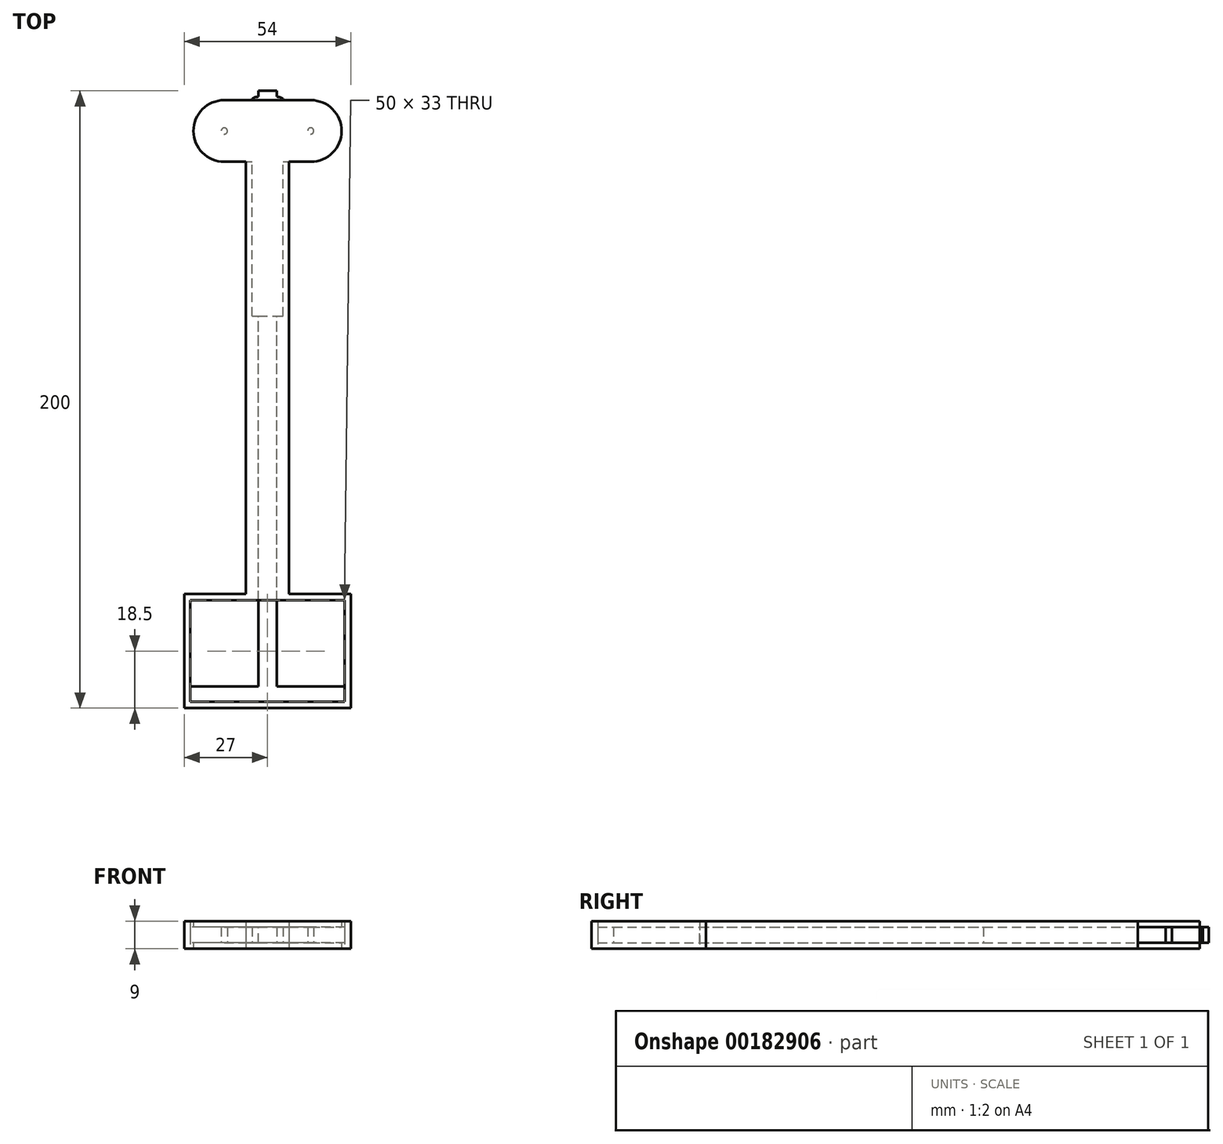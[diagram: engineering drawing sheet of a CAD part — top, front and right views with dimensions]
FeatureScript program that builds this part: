
annotation { "Feature Type Name" : "Feature", "Feature Type Description" : "" }
export const myFeature = defineFeature(function(context is Context, id is Id, definition is map)
    precondition{}
    {
        {
            var Q0;
            Q0=qCreatedBy(makeId("Top.planeOp"),FACE);
            var sketch = newSketch(context, id + "F0", { "sketchPlane" : qUnion([Q0])});
            skLineSegment(sketch, "E0.bottom", {"start": v(0, -180) * mm, "end": v(3, -180) * mm});
            skLineSegment(sketch, "E0.top", {"start": v(0, 13) * mm, "end": v(3, 13) * mm});
            skLineSegment(sketch, "E0.left", {"start": v(0, -180) * mm, "end": v(0, 13) * mm});
            skLineSegment(sketch, "E0.right", {"start": v(3, -180) * mm, "end": v(3, 13) * mm});
            skLineSegment(sketch, "E1", {"start": v(0, 10) * mm, "end": v(3, 10) * mm, "construction": true});
            skArc(sketch, "E2", {"start": v(3, 11.09) * mm, "mid": v(4.04, 10.94) * mm, "end": v(5, 10.5) * mm});
            skLineSegment(sketch, "E3", {"start": v(5, 10.5) * mm, "end": v(5, 10) * mm});
            skPoint(sketch, "E3.endSnap0", {"position": v(1.5, 10) * mm});
            skArc(sketch, "E4.MirrorCS", {"start": v(3, 8.91) * mm, "mid": v(4.04, 9.06) * mm, "end": v(5, 9.5) * mm});
            skLineSegment(sketch, "E5.MirrorCS", {"start": v(5, 9.5) * mm, "end": v(5, 10) * mm});
            skArc(sketch, "E6.1.0.0", {"start": v(3, 7.89) * mm, "mid": v(4.04, 7.74) * mm, "end": v(5, 7.3) * mm});
            skLineSegment(sketch, "E6.1.0.1", {"start": v(5, 7.3) * mm, "end": v(5, 6.8) * mm});
            skLineSegment(sketch, "E6.1.0.2", {"start": v(5, 6.3) * mm, "end": v(5, 6.8) * mm});
            skArc(sketch, "E6.1.0.3", {"start": v(3, 5.71) * mm, "mid": v(4.04, 5.86) * mm, "end": v(5, 6.3) * mm});
            skArc(sketch, "E6.2.0.0", {"start": v(3, 4.69) * mm, "mid": v(4.04, 4.54) * mm, "end": v(5, 4.1) * mm});
            skLineSegment(sketch, "E6.2.0.1", {"start": v(5, 4.1) * mm, "end": v(5, 3.6) * mm});
            skLineSegment(sketch, "E6.2.0.2", {"start": v(5, 3.1) * mm, "end": v(5, 3.6) * mm});
            skArc(sketch, "E6.2.0.3", {"start": v(3, 2.51) * mm, "mid": v(4.04, 2.66) * mm, "end": v(5, 3.1) * mm});
            skLineSegment(sketch, "E6.direction1", {"start": v(3, 7.39) * mm, "end": v(3, 4.19) * mm, "construction": true});
            skArc(sketch, "E7.0.3.0", {"start": v(3, 1.49) * mm, "mid": v(4.04, 1.34) * mm, "end": v(5, 0.9) * mm});
            skLineSegment(sketch, "E7.4.3.0", {"start": v(5, 0.9) * mm, "end": v(5, 0.4) * mm});
            skLineSegment(sketch, "E7.7.3.0", {"start": v(5, -0.1) * mm, "end": v(5, 0.4) * mm});
            skArc(sketch, "E7.10.3.0", {"start": v(3, -0.69) * mm, "mid": v(4.04, -0.54) * mm, "end": v(5, -0.1) * mm});
            skArc(sketch, "E7.0.4.0", {"start": v(3, -1.71) * mm, "mid": v(4.04, -1.86) * mm, "end": v(5, -2.3) * mm});
            skLineSegment(sketch, "E7.4.4.0", {"start": v(5, -2.3) * mm, "end": v(5, -2.8) * mm});
            skLineSegment(sketch, "E7.7.4.0", {"start": v(5, -3.3) * mm, "end": v(5, -2.8) * mm});
            skArc(sketch, "E7.10.4.0", {"start": v(3, -3.89) * mm, "mid": v(4.04, -3.74) * mm, "end": v(5, -3.3) * mm});
            skArc(sketch, "E7.0.5.0", {"start": v(3, -4.91) * mm, "mid": v(4.04, -5.06) * mm, "end": v(5, -5.5) * mm});
            skLineSegment(sketch, "E7.4.5.0", {"start": v(5, -5.5) * mm, "end": v(5, -6) * mm});
            skLineSegment(sketch, "E7.7.5.0", {"start": v(5, -6.5) * mm, "end": v(5, -6) * mm});
            skArc(sketch, "E7.10.5.0", {"start": v(3, -7.09) * mm, "mid": v(4.04, -6.94) * mm, "end": v(5, -6.5) * mm});
            skArc(sketch, "E7.0.6.0", {"start": v(3, -8.11) * mm, "mid": v(4.04, -8.26) * mm, "end": v(5, -8.7) * mm});
            skLineSegment(sketch, "E7.4.6.0", {"start": v(5, -8.7) * mm, "end": v(5, -9.2) * mm});
            skLineSegment(sketch, "E7.7.6.0", {"start": v(5, -9.7) * mm, "end": v(5, -9.2) * mm});
            skArc(sketch, "E7.10.6.0", {"start": v(3, -10.29) * mm, "mid": v(4.04, -10.14) * mm, "end": v(5, -9.7) * mm});
            skArc(sketch, "E7.0.7.0", {"start": v(3, -11.31) * mm, "mid": v(4.04, -11.46) * mm, "end": v(5, -11.9) * mm});
            skLineSegment(sketch, "E7.4.7.0", {"start": v(5, -11.9) * mm, "end": v(5, -12.4) * mm});
            skLineSegment(sketch, "E7.7.7.0", {"start": v(5, -12.9) * mm, "end": v(5, -12.4) * mm});
            skArc(sketch, "E7.10.7.0", {"start": v(3, -13.49) * mm, "mid": v(4.04, -13.34) * mm, "end": v(5, -12.9) * mm});
            skArc(sketch, "E7.0.8.0", {"start": v(3, -14.51) * mm, "mid": v(4.04, -14.66) * mm, "end": v(5, -15.1) * mm});
            skLineSegment(sketch, "E7.4.8.0", {"start": v(5, -15.1) * mm, "end": v(5, -15.6) * mm});
            skLineSegment(sketch, "E7.7.8.0", {"start": v(5, -16.1) * mm, "end": v(5, -15.6) * mm});
            skArc(sketch, "E7.10.8.0", {"start": v(3, -16.69) * mm, "mid": v(4.04, -16.54) * mm, "end": v(5, -16.1) * mm});
            skArc(sketch, "E7.0.9.0", {"start": v(3, -17.71) * mm, "mid": v(4.04, -17.86) * mm, "end": v(5, -18.3) * mm});
            skLineSegment(sketch, "E7.4.9.0", {"start": v(5, -18.3) * mm, "end": v(5, -18.8) * mm});
            skLineSegment(sketch, "E7.7.9.0", {"start": v(5, -19.3) * mm, "end": v(5, -18.8) * mm});
            skArc(sketch, "E7.10.9.0", {"start": v(3, -19.89) * mm, "mid": v(4.04, -19.74) * mm, "end": v(5, -19.3) * mm});
            skArc(sketch, "E7.0.10.0", {"start": v(3, -20.91) * mm, "mid": v(4.04, -21.06) * mm, "end": v(5, -21.5) * mm});
            skLineSegment(sketch, "E7.4.10.0", {"start": v(5, -21.5) * mm, "end": v(5, -22) * mm});
            skLineSegment(sketch, "E7.7.10.0", {"start": v(5, -22.5) * mm, "end": v(5, -22) * mm});
            skArc(sketch, "E7.10.10.0", {"start": v(3, -23.09) * mm, "mid": v(4.04, -22.94) * mm, "end": v(5, -22.5) * mm});
            skArc(sketch, "E7.0.11.0", {"start": v(3, -24.11) * mm, "mid": v(4.04, -24.26) * mm, "end": v(5, -24.7) * mm});
            skLineSegment(sketch, "E7.4.11.0", {"start": v(5, -24.7) * mm, "end": v(5, -25.2) * mm});
            skLineSegment(sketch, "E7.7.11.0", {"start": v(5, -25.7) * mm, "end": v(5, -25.2) * mm});
            skArc(sketch, "E7.10.11.0", {"start": v(3, -26.29) * mm, "mid": v(4.04, -26.14) * mm, "end": v(5, -25.7) * mm});
            skArc(sketch, "E7.0.12.0", {"start": v(3, -27.31) * mm, "mid": v(4.04, -27.46) * mm, "end": v(5, -27.9) * mm});
            skLineSegment(sketch, "E7.4.12.0", {"start": v(5, -27.9) * mm, "end": v(5, -28.4) * mm});
            skLineSegment(sketch, "E7.7.12.0", {"start": v(5, -28.9) * mm, "end": v(5, -28.4) * mm});
            skArc(sketch, "E7.10.12.0", {"start": v(3, -29.49) * mm, "mid": v(4.04, -29.34) * mm, "end": v(5, -28.9) * mm});
            skArc(sketch, "E7.0.13.0", {"start": v(3, -30.51) * mm, "mid": v(4.04, -30.66) * mm, "end": v(5, -31.1) * mm});
            skLineSegment(sketch, "E7.4.13.0", {"start": v(5, -31.1) * mm, "end": v(5, -31.6) * mm});
            skLineSegment(sketch, "E7.7.13.0", {"start": v(5, -32.1) * mm, "end": v(5, -31.6) * mm});
            skArc(sketch, "E7.10.13.0", {"start": v(3, -32.69) * mm, "mid": v(4.04, -32.54) * mm, "end": v(5, -32.1) * mm});
            skArc(sketch, "E7.0.14.0", {"start": v(3, -33.71) * mm, "mid": v(4.04, -33.86) * mm, "end": v(5, -34.3) * mm});
            skLineSegment(sketch, "E7.4.14.0", {"start": v(5, -34.3) * mm, "end": v(5, -34.8) * mm});
            skLineSegment(sketch, "E7.7.14.0", {"start": v(5, -35.3) * mm, "end": v(5, -34.8) * mm});
            skArc(sketch, "E7.10.14.0", {"start": v(3, -35.89) * mm, "mid": v(4.04, -35.74) * mm, "end": v(5, -35.3) * mm});
            skArc(sketch, "E7.0.15.0", {"start": v(3, -36.91) * mm, "mid": v(4.04, -37.06) * mm, "end": v(5, -37.5) * mm});
            skLineSegment(sketch, "E7.4.15.0", {"start": v(5, -37.5) * mm, "end": v(5, -38) * mm});
            skLineSegment(sketch, "E7.7.15.0", {"start": v(5, -38.5) * mm, "end": v(5, -38) * mm});
            skArc(sketch, "E7.10.15.0", {"start": v(3, -39.09) * mm, "mid": v(4.04, -38.94) * mm, "end": v(5, -38.5) * mm});
            skSolve(sketch);
        }
        {
            var Q0;
            Q0 = qSketchRegion(id + "F0", true);
            extrude(context, id + "F1", {"entities" : qUnion([Q0]), "depth" : 5 * mm});
        }
        {
            var Q0;
            Q0=makeQuery(id+"F1.opExtrude","SWEPT_BODY",BODY,{"disambiguationData":[OSD([sQuery(id+"F0.wireOp",EDGE,"E0.bottom"),sQuery(id+"F0.wireOp",EDGE,"E0.top"),sQuery(id+"F0.wireOp",EDGE,"E0.left"),sQuery(id+"F0.wireOp",EDGE,"E0.right"),sQuery(id+"F0.wireOp",EDGE,"E2"),sQuery(id+"F0.wireOp",EDGE,"E3"),sQuery(id+"F0.wireOp",EDGE,"E4.MirrorCS"),sQuery(id+"F0.wireOp",EDGE,"E5.MirrorCS"),sQuery(id+"F0.wireOp",EDGE,"E6.1.0.0"),sQuery(id+"F0.wireOp",EDGE,"E6.1.0.1"),sQuery(id+"F0.wireOp",EDGE,"E6.1.0.2"),sQuery(id+"F0.wireOp",EDGE,"E6.1.0.3"),sQuery(id+"F0.wireOp",EDGE,"E6.2.0.0"),sQuery(id+"F0.wireOp",EDGE,"E6.2.0.1"),sQuery(id+"F0.wireOp",EDGE,"E6.2.0.2"),sQuery(id+"F0.wireOp",EDGE,"E6.2.0.3"),sQuery(id+"F0.wireOp",EDGE,"E7.0.3.0"),sQuery(id+"F0.wireOp",EDGE,"E7.4.3.0"),sQuery(id+"F0.wireOp",EDGE,"E7.7.3.0"),sQuery(id+"F0.wireOp",EDGE,"E7.10.3.0"),sQuery(id+"F0.wireOp",EDGE,"E7.0.4.0"),sQuery(id+"F0.wireOp",EDGE,"E7.4.4.0"),sQuery(id+"F0.wireOp",EDGE,"E7.7.4.0"),sQuery(id+"F0.wireOp",EDGE,"E7.10.4.0"),sQuery(id+"F0.wireOp",EDGE,"E7.0.5.0"),sQuery(id+"F0.wireOp",EDGE,"E7.4.5.0"),sQuery(id+"F0.wireOp",EDGE,"E7.7.5.0"),sQuery(id+"F0.wireOp",EDGE,"E7.10.5.0"),sQuery(id+"F0.wireOp",EDGE,"E7.0.6.0"),sQuery(id+"F0.wireOp",EDGE,"E7.4.6.0"),sQuery(id+"F0.wireOp",EDGE,"E7.7.6.0"),sQuery(id+"F0.wireOp",EDGE,"E7.10.6.0"),sQuery(id+"F0.wireOp",EDGE,"E7.0.7.0"),sQuery(id+"F0.wireOp",EDGE,"E7.4.7.0"),sQuery(id+"F0.wireOp",EDGE,"E7.7.7.0"),sQuery(id+"F0.wireOp",EDGE,"E7.10.7.0"),sQuery(id+"F0.wireOp",EDGE,"E7.0.8.0"),sQuery(id+"F0.wireOp",EDGE,"E7.4.8.0"),sQuery(id+"F0.wireOp",EDGE,"E7.7.8.0"),sQuery(id+"F0.wireOp",EDGE,"E7.10.8.0"),sQuery(id+"F0.wireOp",EDGE,"E7.0.9.0"),sQuery(id+"F0.wireOp",EDGE,"E7.4.9.0"),sQuery(id+"F0.wireOp",EDGE,"E7.7.9.0"),sQuery(id+"F0.wireOp",EDGE,"E7.10.9.0"),sQuery(id+"F0.wireOp",EDGE,"E7.0.10.0"),sQuery(id+"F0.wireOp",EDGE,"E7.4.10.0"),sQuery(id+"F0.wireOp",EDGE,"E7.7.10.0"),sQuery(id+"F0.wireOp",EDGE,"E7.10.10.0"),sQuery(id+"F0.wireOp",EDGE,"E7.0.11.0"),sQuery(id+"F0.wireOp",EDGE,"E7.4.11.0"),sQuery(id+"F0.wireOp",EDGE,"E7.7.11.0"),sQuery(id+"F0.wireOp",EDGE,"E7.10.11.0"),sQuery(id+"F0.wireOp",EDGE,"E7.0.12.0"),sQuery(id+"F0.wireOp",EDGE,"E7.4.12.0"),sQuery(id+"F0.wireOp",EDGE,"E7.7.12.0"),sQuery(id+"F0.wireOp",EDGE,"E7.10.12.0"),sQuery(id+"F0.wireOp",EDGE,"E7.0.13.0"),sQuery(id+"F0.wireOp",EDGE,"E7.4.13.0"),sQuery(id+"F0.wireOp",EDGE,"E7.7.13.0"),sQuery(id+"F0.wireOp",EDGE,"E7.10.13.0"),sQuery(id+"F0.wireOp",EDGE,"E7.0.14.0"),sQuery(id+"F0.wireOp",EDGE,"E7.4.14.0"),sQuery(id+"F0.wireOp",EDGE,"E7.7.14.0"),sQuery(id+"F0.wireOp",EDGE,"E7.10.14.0"),sQuery(id+"F0.wireOp",EDGE,"E7.0.15.0"),sQuery(id+"F0.wireOp",EDGE,"E7.4.15.0"),sQuery(id+"F0.wireOp",EDGE,"E7.7.15.0"),sQuery(id+"F0.wireOp",EDGE,"E7.10.15.0")])]});
            var Q1;
            Q1=makeQuery(id+"F1.opExtrude","SWEPT_FACE",FACE,{"disambiguationData":[OSD([sQuery(id+"F0.wireOp",EDGE,"E0.left")])]});
            mirror(context, id + "F2", {"operationType" : NewBodyOperationType.ADD, "entities" : qUnion([Q0]), "mirrorPlane" : qUnion([Q1])});
        }
        {
            var Q0;
            {var subQ0=makeQuery(id+"F1.opExtrude","SWEPT_FACE",FACE,{"disambiguationData":[OSD([sQuery(id+"F0.wireOp",EDGE,"E0.bottom")])]});Q0=makeQuery(id+"F2.boolean.opBoolean","MERGE",FACE,{"derivedFrom":[subQ0,makeQuery(id+"F2.opPattern","COPY",FACE,{"derivedFrom":subQ0,"instanceName":"1"})]});}
            var sketch = newSketch(context, id + "F3", { "sketchPlane" : qUnion([Q0])});
            skLineSegment(sketch, "E8.bottom", {"start": v(25, 5) * mm, "end": v(-25, 5) * mm});
            skLineSegment(sketch, "E8.top", {"start": v(25, 0) * mm, "end": v(-25, 0) * mm});
            skLineSegment(sketch, "E8.left", {"start": v(25, 5) * mm, "end": v(25, 0) * mm});
            skLineSegment(sketch, "E8.right", {"start": v(-25, 5) * mm, "end": v(-25, 0) * mm});
            skPoint(sketch, "E8.middle", {"position": v(0, 2.5) * mm});
            skPoint(sketch, "E8.middle.positionSnap0", {"position": v(-3, 2.5) * mm});
            skPoint(sketch, "E8.centerSnap0", {"position": v(-3, 2.5) * mm});
            skSolve(sketch);
        }
        {
            var Q0;
            Q0 = qSketchRegion(id + "F3", true);
            extrude(context, id + "F4", {"entities" : qUnion([Q0]), "operationType" : NewBodyOperationType.ADD, "depth" : 5 * mm});
        }
        {
            var Q0;
            Q0=qCreatedBy(makeId("Top.planeOp"),FACE);
            var sketch = newSketch(context, id + "F5", { "sketchPlane" : qUnion([Q0])});
            skCircle(sketch, "E9", {"center": v(14, 0) * mm, "radius": 10 * mm});
            skLineSegment(sketch, "E10", {"start": v(14, 10) * mm, "end": v(0, 10) * mm});
            skLineSegment(sketch, "E11", {"start": v(14, -10) * mm, "end": v(7, -10) * mm});
            skLineSegment(sketch, "E12", {"start": v(7, -10) * mm, "end": v(7, -150) * mm});
            skLineSegment(sketch, "E13", {"start": v(7, -150) * mm, "end": v(27, -150) * mm});
            skLineSegment(sketch, "E14", {"start": v(27, -150) * mm, "end": v(27, -187) * mm});
            skLineSegment(sketch, "E15", {"start": v(27, -187) * mm, "end": v(0, -187) * mm});
            skLineSegment(sketch, "E16.MirrorCS", {"start": v(-14, 10) * mm, "end": v(0, 10) * mm});
            skCircle(sketch, "E17.MirrorC", {"center": v(-14, 0) * mm, "radius": 10 * mm});
            skLineSegment(sketch, "E18.MirrorCS", {"start": v(-14, -10) * mm, "end": v(-7, -10) * mm});
            skLineSegment(sketch, "E19.MirrorCS", {"start": v(-7, -10) * mm, "end": v(-7, -150) * mm});
            skLineSegment(sketch, "E20.MirrorCS", {"start": v(-7, -150) * mm, "end": v(-27, -150) * mm});
            skLineSegment(sketch, "E21.MirrorCS", {"start": v(-27, -150) * mm, "end": v(-27, -187) * mm});
            skLineSegment(sketch, "E22.MirrorCS", {"start": v(-27, -187) * mm, "end": v(0, -187) * mm});
            skLineSegment(sketch, "E23.bottom", {"start": v(-25, -152) * mm, "end": v(25, -152) * mm});
            skLineSegment(sketch, "E23.top", {"start": v(-25, -185) * mm, "end": v(25, -185) * mm});
            skLineSegment(sketch, "E23.left", {"start": v(-25, -152) * mm, "end": v(-25, -185) * mm});
            skLineSegment(sketch, "E23.right", {"start": v(25, -152) * mm, "end": v(25, -185) * mm});
            skPoint(sketch, "E23.middle", {"position": v(0, -168.5) * mm});
            skSolve(sketch);
        }
        {
            var Q0;
            Q0 = qSketchRegion(id + "F5", true);
            extrude(context, id + "F6", {"entities" : qUnion([Q0]), "depth" : 7 * mm, "hasSecondDirection" : true, "secondDirectionOppositeDirection" : true, "secondDirectionDepth" : 2 * mm});
        }
        {
            var Q0;
            Q0=makeQuery(id+"F1.opExtrude","SWEPT_BODY",BODY,{"disambiguationData":[OSD([sQuery(id+"F0.wireOp",EDGE,"E0.bottom"),sQuery(id+"F0.wireOp",EDGE,"E0.top"),sQuery(id+"F0.wireOp",EDGE,"E0.left"),sQuery(id+"F0.wireOp",EDGE,"E0.right"),sQuery(id+"F0.wireOp",EDGE,"E2"),sQuery(id+"F0.wireOp",EDGE,"E3"),sQuery(id+"F0.wireOp",EDGE,"E4.MirrorCS"),sQuery(id+"F0.wireOp",EDGE,"E5.MirrorCS"),sQuery(id+"F0.wireOp",EDGE,"E6.1.0.0"),sQuery(id+"F0.wireOp",EDGE,"E6.1.0.1"),sQuery(id+"F0.wireOp",EDGE,"E6.1.0.2"),sQuery(id+"F0.wireOp",EDGE,"E6.1.0.3"),sQuery(id+"F0.wireOp",EDGE,"E6.2.0.0"),sQuery(id+"F0.wireOp",EDGE,"E6.2.0.1"),sQuery(id+"F0.wireOp",EDGE,"E6.2.0.2"),sQuery(id+"F0.wireOp",EDGE,"E6.2.0.3"),sQuery(id+"F0.wireOp",EDGE,"E7.0.3.0"),sQuery(id+"F0.wireOp",EDGE,"E7.4.3.0"),sQuery(id+"F0.wireOp",EDGE,"E7.7.3.0"),sQuery(id+"F0.wireOp",EDGE,"E7.10.3.0"),sQuery(id+"F0.wireOp",EDGE,"E7.0.4.0"),sQuery(id+"F0.wireOp",EDGE,"E7.4.4.0"),sQuery(id+"F0.wireOp",EDGE,"E7.7.4.0"),sQuery(id+"F0.wireOp",EDGE,"E7.10.4.0"),sQuery(id+"F0.wireOp",EDGE,"E7.0.5.0"),sQuery(id+"F0.wireOp",EDGE,"E7.4.5.0"),sQuery(id+"F0.wireOp",EDGE,"E7.7.5.0"),sQuery(id+"F0.wireOp",EDGE,"E7.10.5.0"),sQuery(id+"F0.wireOp",EDGE,"E7.0.6.0"),sQuery(id+"F0.wireOp",EDGE,"E7.4.6.0"),sQuery(id+"F0.wireOp",EDGE,"E7.7.6.0"),sQuery(id+"F0.wireOp",EDGE,"E7.10.6.0"),sQuery(id+"F0.wireOp",EDGE,"E7.0.7.0"),sQuery(id+"F0.wireOp",EDGE,"E7.4.7.0"),sQuery(id+"F0.wireOp",EDGE,"E7.7.7.0"),sQuery(id+"F0.wireOp",EDGE,"E7.10.7.0"),sQuery(id+"F0.wireOp",EDGE,"E7.0.8.0"),sQuery(id+"F0.wireOp",EDGE,"E7.4.8.0"),sQuery(id+"F0.wireOp",EDGE,"E7.7.8.0"),sQuery(id+"F0.wireOp",EDGE,"E7.10.8.0"),sQuery(id+"F0.wireOp",EDGE,"E7.0.9.0"),sQuery(id+"F0.wireOp",EDGE,"E7.4.9.0"),sQuery(id+"F0.wireOp",EDGE,"E7.7.9.0"),sQuery(id+"F0.wireOp",EDGE,"E7.10.9.0"),sQuery(id+"F0.wireOp",EDGE,"E7.0.10.0"),sQuery(id+"F0.wireOp",EDGE,"E7.4.10.0"),sQuery(id+"F0.wireOp",EDGE,"E7.7.10.0"),sQuery(id+"F0.wireOp",EDGE,"E7.10.10.0"),sQuery(id+"F0.wireOp",EDGE,"E7.0.11.0"),sQuery(id+"F0.wireOp",EDGE,"E7.4.11.0"),sQuery(id+"F0.wireOp",EDGE,"E7.7.11.0"),sQuery(id+"F0.wireOp",EDGE,"E7.10.11.0"),sQuery(id+"F0.wireOp",EDGE,"E7.0.12.0"),sQuery(id+"F0.wireOp",EDGE,"E7.4.12.0"),sQuery(id+"F0.wireOp",EDGE,"E7.7.12.0"),sQuery(id+"F0.wireOp",EDGE,"E7.10.12.0"),sQuery(id+"F0.wireOp",EDGE,"E7.0.13.0"),sQuery(id+"F0.wireOp",EDGE,"E7.4.13.0"),sQuery(id+"F0.wireOp",EDGE,"E7.7.13.0"),sQuery(id+"F0.wireOp",EDGE,"E7.10.13.0"),sQuery(id+"F0.wireOp",EDGE,"E7.0.14.0"),sQuery(id+"F0.wireOp",EDGE,"E7.4.14.0"),sQuery(id+"F0.wireOp",EDGE,"E7.7.14.0"),sQuery(id+"F0.wireOp",EDGE,"E7.10.14.0"),sQuery(id+"F0.wireOp",EDGE,"E7.0.15.0"),sQuery(id+"F0.wireOp",EDGE,"E7.4.15.0"),sQuery(id+"F0.wireOp",EDGE,"E7.7.15.0"),sQuery(id+"F0.wireOp",EDGE,"E7.10.15.0")])]});
            var Q1;
            Q1=makeQuery(id+"F6.opExtrude","SWEPT_BODY",BODY,{"disambiguationData":[OSD([sQuery(id+"F5.wireOp",EDGE,"E9"),sQuery(id+"F5.wireOp",EDGE,"E10"),sQuery(id+"F5.wireOp",EDGE,"E11"),sQuery(id+"F5.wireOp",EDGE,"E12"),sQuery(id+"F5.wireOp",EDGE,"E13"),sQuery(id+"F5.wireOp",EDGE,"E14"),sQuery(id+"F5.wireOp",EDGE,"E15"),sQuery(id+"F5.wireOp",EDGE,"E16.MirrorCS"),sQuery(id+"F5.wireOp",EDGE,"E17.MirrorC"),sQuery(id+"F5.wireOp",EDGE,"E18.MirrorCS"),sQuery(id+"F5.wireOp",EDGE,"E19.MirrorCS"),sQuery(id+"F5.wireOp",EDGE,"E20.MirrorCS"),sQuery(id+"F5.wireOp",EDGE,"E21.MirrorCS"),sQuery(id+"F5.wireOp",EDGE,"E22.MirrorCS"),sQuery(id+"F5.wireOp",EDGE,"E23.bottom"),sQuery(id+"F5.wireOp",EDGE,"E23.top"),sQuery(id+"F5.wireOp",EDGE,"E23.left"),sQuery(id+"F5.wireOp",EDGE,"E23.right")])]});
            booleanBodies(context, id + "F7", {"operationType" : BooleanOperationType.SUBTRACTION, "tools" : qUnion([Q0]), "targets" : qUnion([Q1]), "keepTools" : true});
        }
        {
            var Q0;
            Q0=qCreatedBy(makeId("Top.planeOp"),FACE);
            var sketch = newSketch(context, id + "F8", { "sketchPlane" : qUnion([Q0])});
            skArc(sketch, "E24.0", {"start": v(-14, -10) * mm, "mid": v(-24, 0) * mm, "end": v(-14, 10) * mm});
            skPoint(sketch, "E25.0", {"position": v(24, 0) * mm});
            skLineSegment(sketch, "E26.0", {"start": v(14, 10) * mm, "end": v(-14, 10) * mm});
            skArc(sketch, "E27.0", {"start": v(14, -10) * mm, "mid": v(24, 0) * mm, "end": v(14, 10) * mm});
            skLineSegment(sketch, "E28", {"start": v(-14, -10) * mm, "end": v(14, -10) * mm});
            skSolve(sketch);
        }
        {
            var Q0;
            Q0 = qSketchRegion(id + "F8", true);
            extrude(context, id + "F9", {"entities" : qUnion([Q0]), "operationType" : NewBodyOperationType.REMOVE, "depth" : 5 * mm});
        }
        {
            var Q0;
            {var subQ70=sQuery(id+"F8.wireOp",EDGE,"E28");Q0=makeQuery(id+"F9.boolean.opBoolean","COPY",FACE,{"disambiguationData":[TD([makeQuery(id+"F6.opExtrude","SWEPT_FACE",FACE,{"disambiguationData":[OSD([sQuery(id+"F5.wireOp",EDGE,"E11")])]})])],"derivedFrom":makeQuery(id+"F9.opExtrude","SWEPT_FACE",FACE,{"disambiguationData":[OSD([subQ70])]})});}
            var sketch = newSketch(context, id + "F10", { "sketchPlane" : qUnion([Q0])});
            skLineSegment(sketch, "E29.bottom", {"start": v(5, 5) * mm, "end": v(-5, 5) * mm});
            skLineSegment(sketch, "E29.top", {"start": v(5, 0) * mm, "end": v(-5, 0) * mm});
            skLineSegment(sketch, "E29.left", {"start": v(5, 5) * mm, "end": v(5, 0) * mm});
            skLineSegment(sketch, "E29.right", {"start": v(-5, 5) * mm, "end": v(-5, 0) * mm});
            skSolve(sketch);
        }
        {
            var Q0;
            Q0 = qSketchRegion(id + "F10", true);
            extrude(context, id + "F11", {"entities" : qUnion([Q0]), "operationType" : NewBodyOperationType.REMOVE, "oppositeDirection" : true, "depth" : 50 * mm});
        }
        {
            var Q0;
            Q0=qCreatedBy(makeId("Top.planeOp"),FACE);
            var sketch = newSketch(context, id + "F12", { "sketchPlane" : qUnion([Q0])});
            skCircle(sketch, "E30", {"center": v(-14, 0) * mm, "radius": 1 * mm});
            skCircle(sketch, "E31", {"center": v(14, 0) * mm, "radius": 1 * mm});
            skSolve(sketch);
        }
        {
            var Q0;
            Q0 = qSketchRegion(id + "F12", true);
            extrude(context, id + "F13", {"entities" : qUnion([Q0]), "operationType" : NewBodyOperationType.ADD, "endBound" : BoundingType.UP_TO_NEXT, "depth" : 25 * mm});
        }
    });
